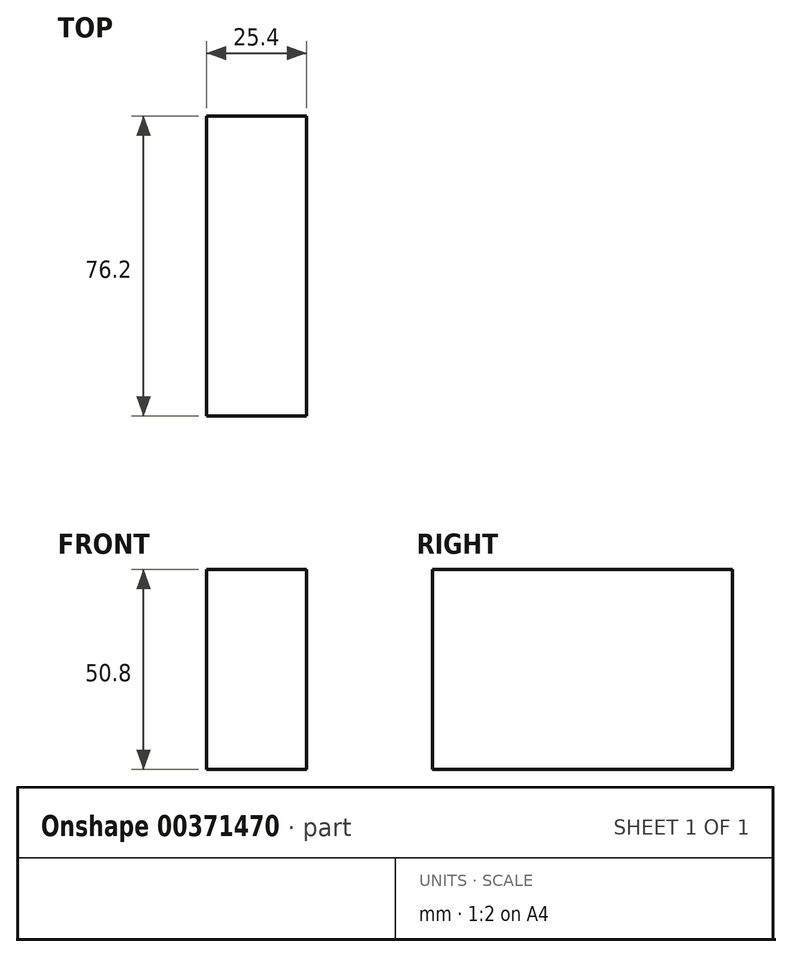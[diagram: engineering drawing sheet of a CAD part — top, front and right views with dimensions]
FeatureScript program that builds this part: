
annotation { "Feature Type Name" : "Feature", "Feature Type Description" : "" }
export const myFeature = defineFeature(function(context is Context, id is Id, definition is map)
    precondition{}
    {
        {
            var Q0;
            Q0=qCreatedBy(makeId("Right.planeOp"),FACE);
            var sketch = newSketch(context, id + "F0", { "sketchPlane" : qUnion([Q0])});
            skLineSegment(sketch, "E0.bottom", {"start": v(38.1, 25.4) * mm, "end": v(-38.1, 25.4) * mm});
            skLineSegment(sketch, "E0.top", {"start": v(38.1, -25.4) * mm, "end": v(-38.1, -25.4) * mm});
            skLineSegment(sketch, "E0.left", {"start": v(38.1, 25.4) * mm, "end": v(38.1, -25.4) * mm});
            skLineSegment(sketch, "E0.right", {"start": v(-38.1, 25.4) * mm, "end": v(-38.1, -25.4) * mm});
            skPoint(sketch, "E0.middle", {"position": v(0, 0) * mm});
            skSolve(sketch);
        }
        {
            var Q0;
            Q0 = qSketchRegion(id + "F0", true);
            extrude(context, id + "F1", {"entities" : qUnion([Q0]), "endBound" : BoundingType.SYMMETRIC, "depth" : 25.4 * mm});
        }
    });
